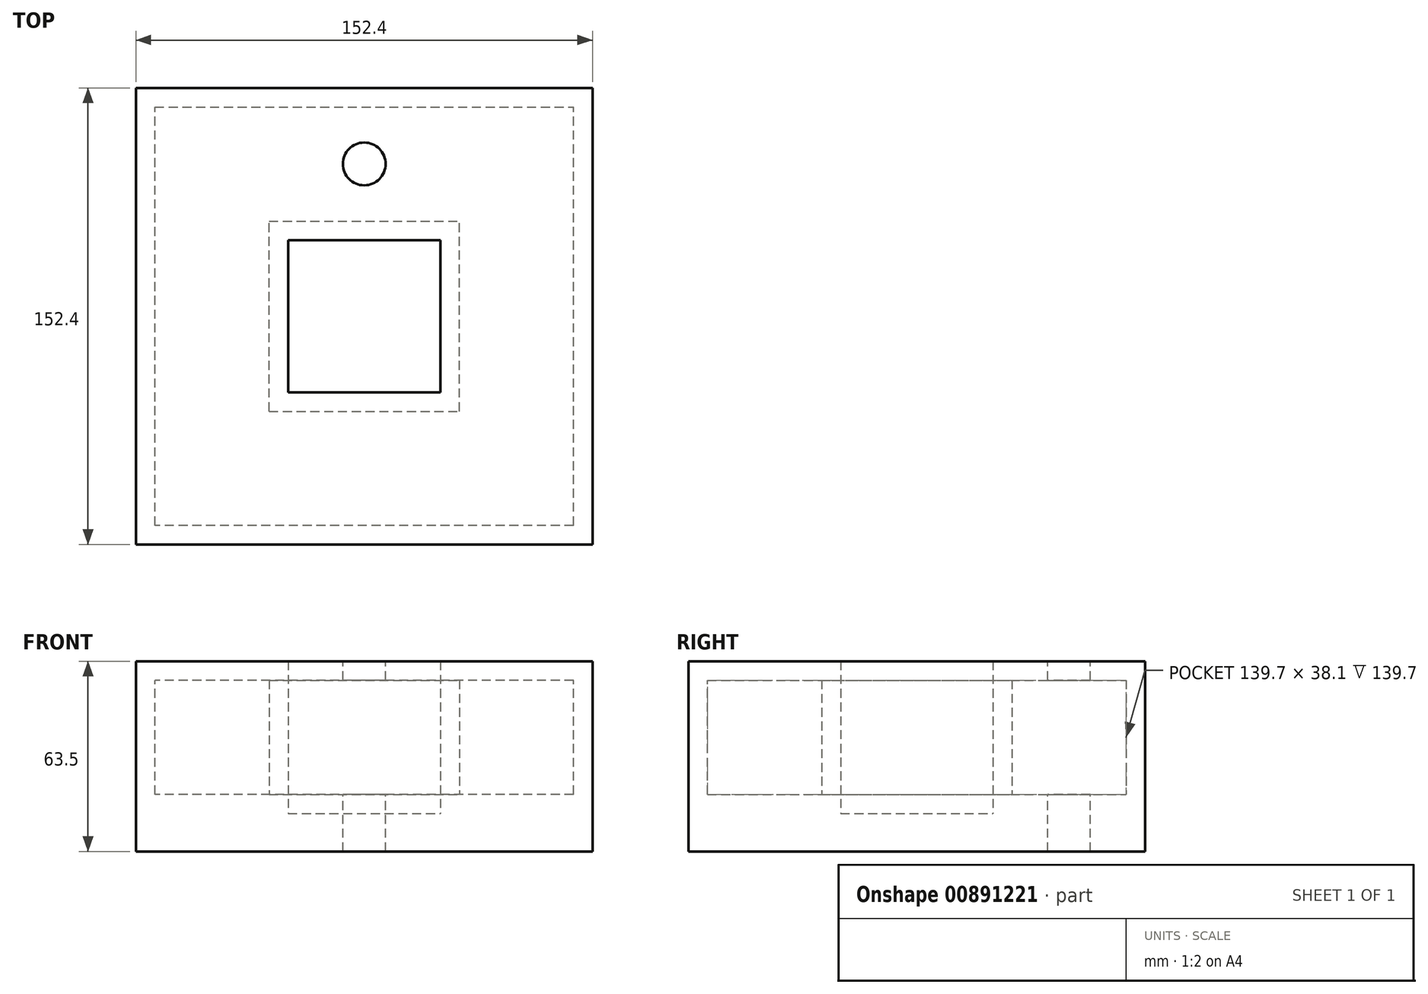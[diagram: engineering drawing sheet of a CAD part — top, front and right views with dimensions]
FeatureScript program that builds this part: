
annotation { "Feature Type Name" : "Feature", "Feature Type Description" : "" }
export const myFeature = defineFeature(function(context is Context, id is Id, definition is map)
    precondition{}
    {
        {
            var Q0;
            Q0=qCreatedBy(makeId("Top.planeOp"),FACE);
            var sketch = newSketch(context, id + "F0", { "sketchPlane" : qUnion([Q0])});
            skLineSegment(sketch, "E0.bottom", {"start": v(0, 0) * mm, "end": v(152.4, 0) * mm});
            skLineSegment(sketch, "E0.top", {"start": v(0, 152.4) * mm, "end": v(152.4, 152.4) * mm});
            skLineSegment(sketch, "E0.left", {"start": v(0, 0) * mm, "end": v(0, 152.4) * mm});
            skLineSegment(sketch, "E0.right", {"start": v(152.4, 0) * mm, "end": v(152.4, 152.4) * mm});
            skLineSegment(sketch, "E1.bottom", {"start": v(50.8, 50.8) * mm, "end": v(101.6, 50.8) * mm});
            skLineSegment(sketch, "E1.top", {"start": v(50.8, 101.6) * mm, "end": v(101.6, 101.6) * mm});
            skLineSegment(sketch, "E1.left", {"start": v(50.8, 50.8) * mm, "end": v(50.8, 101.6) * mm});
            skLineSegment(sketch, "E1.right", {"start": v(101.6, 50.8) * mm, "end": v(101.6, 101.6) * mm});
            skSolve(sketch);
        }
        {
            var Q0;
            Q0 = qSketchRegion(id + "F0", true);
            extrude(context, id + "F1", {"entities" : qUnion([Q0]), "depth" : 50.8 * mm, "offsetDistance" : 25.4 * mm});
        }
        {
            var Q0;
            Q0=makeQuery(id+"F1.opExtrude","SWEPT_FACE",FACE,{"disambiguationData":[OSD([sQuery(id+"F0.wireOp",EDGE,"E0.bottom")])]});
            shell(context, id + "F2", {"entities" : qUnion([Q0]), "thickness" : 6.35 * mm});
        }
        {
            var Q0;
            Q0=makeQuery(id+"F2.opShell","OFFSET_FACE",FACE,{"disambiguationData":[OSD([sQuery(id+"F0.wireOp",EDGE,"E0.left")])]});
            var sketch = newSketch(context, id + "F3", { "sketchPlane" : qUnion([Q0])});
            skLineSegment(sketch, "E2", {"start": v(0, 6.35) * mm, "end": v(6.35, 6.35) * mm});
            skLineSegment(sketch, "E3", {"start": v(6.35, 6.35) * mm, "end": v(6.35, 44.45) * mm});
            skLineSegment(sketch, "E4", {"start": v(6.35, 44.45) * mm, "end": v(0, 44.45) * mm});
            skLineSegment(sketch, "E5", {"start": v(0, 44.45) * mm, "end": v(0, 6.35) * mm});
            skSolve(sketch);
        }
        {
            var Q0;
            Q0 = qSketchRegion(id + "F3", true);
            extrude(context, id + "F4", {"entities" : qUnion([Q0]), "operationType" : NewBodyOperationType.ADD, "depth" : 139.7 * mm, "offsetDistance" : 25.4 * mm});
        }
        {
            var Q0;
            Q0=makeQuery(id+"F1.opExtrude","CAP_FACE",FACE,{"disambiguationData":[OSD([sQuery(id+"F0.wireOp",EDGE,"E0.bottom"),sQuery(id+"F0.wireOp",EDGE,"E0.top"),sQuery(id+"F0.wireOp",EDGE,"E0.left"),sQuery(id+"F0.wireOp",EDGE,"E0.right"),sQuery(id+"F0.wireOp",EDGE,"E1.bottom"),sQuery(id+"F0.wireOp",EDGE,"E1.top"),sQuery(id+"F0.wireOp",EDGE,"E1.left"),sQuery(id+"F0.wireOp",EDGE,"E1.right")])],"isStart":true});
            var sketch = newSketch(context, id + "F5", { "sketchPlane" : qUnion([Q0])});
            skLineSegment(sketch, "E6.bottom", {"start": v(0, 0) * mm, "end": v(152.4, 0) * mm});
            skLineSegment(sketch, "E6.top", {"start": v(0, -152.4) * mm, "end": v(152.4, -152.4) * mm});
            skLineSegment(sketch, "E6.left", {"start": v(0, 0) * mm, "end": v(0, -152.4) * mm});
            skLineSegment(sketch, "E6.right", {"start": v(152.4, 0) * mm, "end": v(152.4, -152.4) * mm});
            skSolve(sketch);
        }
        {
            var Q0;
            Q0 = qSketchRegion(id + "F5", true);
            extrude(context, id + "F6", {"entities" : qUnion([Q0]), "operationType" : NewBodyOperationType.ADD, "depth" : 12.7 * mm, "offsetDistance" : 25.4 * mm});
        }
        {
            var Q0;
            Q0=makeQuery(id+"F1.opExtrude","CAP_FACE",FACE,{"disambiguationData":[OSD([sQuery(id+"F0.wireOp",EDGE,"E0.bottom"),sQuery(id+"F0.wireOp",EDGE,"E0.top"),sQuery(id+"F0.wireOp",EDGE,"E0.left"),sQuery(id+"F0.wireOp",EDGE,"E0.right"),sQuery(id+"F0.wireOp",EDGE,"E1.bottom"),sQuery(id+"F0.wireOp",EDGE,"E1.top"),sQuery(id+"F0.wireOp",EDGE,"E1.left"),sQuery(id+"F0.wireOp",EDGE,"E1.right")])],"isStart":false});
            var sketch = newSketch(context, id + "F7", { "sketchPlane" : qUnion([Q0])});
            skCircle(sketch, "E7", {"center": v(76.2, 127) * mm, "radius": 7.14 * mm});
            skPoint(sketch, "E7.centerSnap0", {"position": v(76.2, 152.4) * mm});
            skSolve(sketch);
        }
        {
            var Q0;
            Q0 = qSketchRegion(id + "F7", true);
            extrude(context, id + "F8", {"entities" : qUnion([Q0]), "operationType" : NewBodyOperationType.REMOVE, "oppositeDirection" : true, "depth" : 76.2 * mm, "offsetDistance" : 25.4 * mm});
        }
    });
